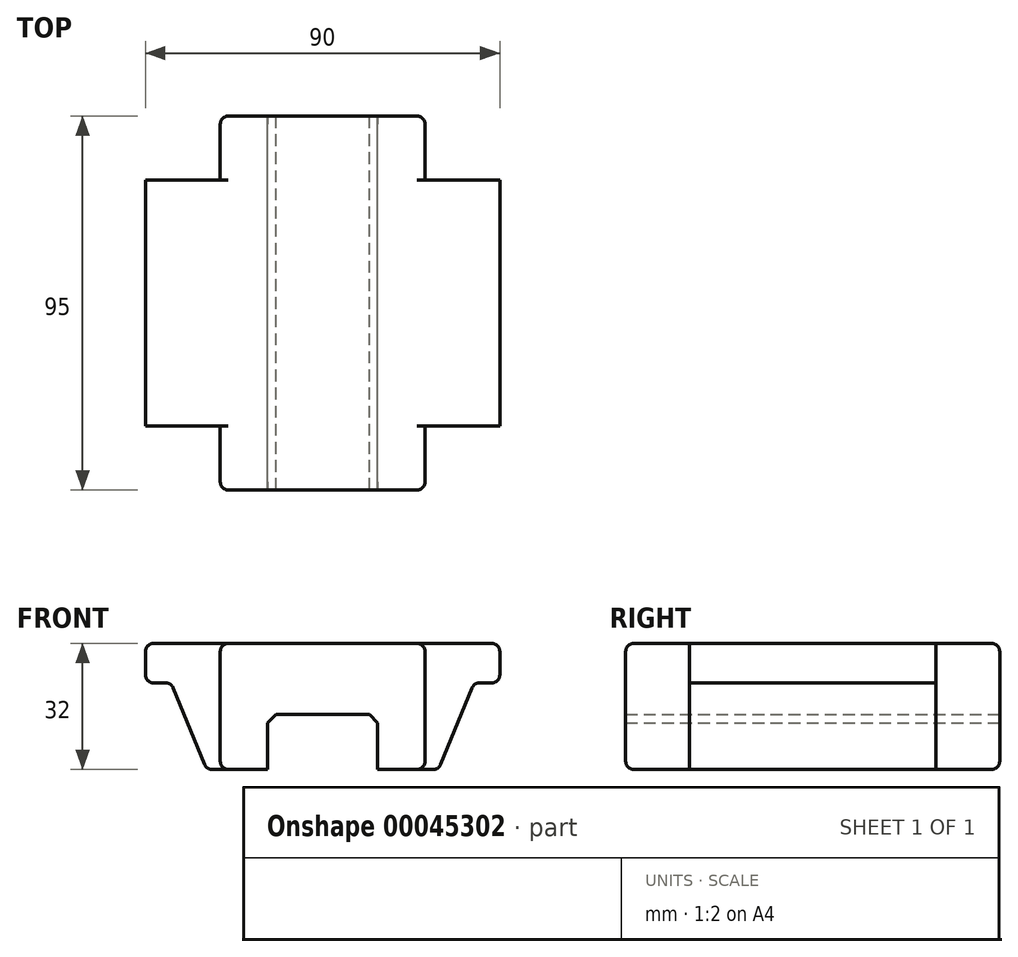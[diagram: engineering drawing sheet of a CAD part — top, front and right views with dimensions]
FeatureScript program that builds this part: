
annotation { "Feature Type Name" : "Feature", "Feature Type Description" : "" }
export const myFeature = defineFeature(function(context is Context, id is Id, definition is map)
    precondition{}
    {
        {
            var Q0;
            Q0=qCreatedBy(makeId("Front.planeOp"),FACE);
            var sketch = newSketch(context, id + "F0", { "sketchPlane" : qUnion([Q0])});
            skLineSegment(sketch, "E0.bottom", {"start": v(-47.43, 10.94) * mm, "end": v(42.57, 10.94) * mm});
            skLineSegment(sketch, "E0.top", {"start": v(-47.43, -21.06) * mm, "end": v(42.57, -21.06) * mm});
            skLineSegment(sketch, "E0.left", {"start": v(-47.43, 10.94) * mm, "end": v(-47.43, -21.06) * mm});
            skLineSegment(sketch, "E0.right", {"start": v(42.57, 10.94) * mm, "end": v(42.57, -21.06) * mm});
            skSolve(sketch);
        }
        {
            var Q0;
            Q0 = qSketchRegion(id + "F0", true);
            extrude(context, id + "F1", {"entities" : qUnion([Q0]), "depth" : 65.2 * mm});
        }
        {
            var Q0;
            Q0=makeQuery(id+"F1.opExtrude","CAP_FACE",FACE,{"disambiguationData":[OSD([sQuery(id+"F0.wireOp",EDGE,"E0.bottom"),sQuery(id+"F0.wireOp",EDGE,"E0.top"),sQuery(id+"F0.wireOp",EDGE,"E0.left"),sQuery(id+"F0.wireOp",EDGE,"E0.right")])],"isStart":false});
            var sketch = newSketch(context, id + "F2", { "sketchPlane" : qUnion([Q0])});
            skLineSegment(sketch, "E1.bottom", {"start": v(-45.43, 10.94) * mm, "end": v(40.57, 10.94) * mm});
            skLineSegment(sketch, "E1.top", {"start": v(-45.43, 0.94) * mm, "end": v(-42.27, 0.94) * mm});
            skLineSegment(sketch, "E1.left", {"start": v(-47.43, 8.94) * mm, "end": v(-47.43, 2.94) * mm});
            skLineSegment(sketch, "E1.right", {"start": v(42.57, 8.94) * mm, "end": v(42.57, 2.94) * mm});
            skLineSegment(sketch, "E2.top", {"start": v(-30.59, -21.06) * mm, "end": v(25.73, -21.06) * mm});
            skLineSegment(sketch, "E3", {"start": v(-40.42, -0.3) * mm, "end": v(-32.44, -19.82) * mm});
            skLineSegment(sketch, "E4", {"start": v(27.58, -19.82) * mm, "end": v(35.56, -0.3) * mm});
            skLineSegment(sketch, "E5.trimOffspring", {"start": v(37.41, 0.94) * mm, "end": v(40.57, 0.94) * mm});
            skPoint(sketch, "E6.visualSharp", {"position": v(42.57, 0.94) * mm});
            skArc(sketch, "E6.filletArc", {"start": v(40.57, 0.94) * mm, "mid": v(41.98, 1.53) * mm, "end": v(42.57, 2.94) * mm});
            skPoint(sketch, "E7.visualSharp", {"position": v(42.57, 10.94) * mm});
            skArc(sketch, "E7.filletArc", {"start": v(42.57, 8.94) * mm, "mid": v(41.98, 10.36) * mm, "end": v(40.57, 10.94) * mm});
            skPoint(sketch, "E8.visualSharp", {"position": v(36.07, 0.94) * mm});
            skArc(sketch, "E8.filletArc", {"start": v(37.41, 0.94) * mm, "mid": v(36.3, 0.6) * mm, "end": v(35.56, -0.3) * mm});
            skPoint(sketch, "E9.visualSharp", {"position": v(27.07, -21.06) * mm});
            skArc(sketch, "E9.filletArc", {"start": v(25.73, -21.06) * mm, "mid": v(26.84, -20.72) * mm, "end": v(27.58, -19.82) * mm});
            skPoint(sketch, "E10.visualSharp", {"position": v(-31.93, -21.06) * mm});
            skArc(sketch, "E10.filletArc", {"start": v(-32.44, -19.82) * mm, "mid": v(-31.7, -20.72) * mm, "end": v(-30.59, -21.06) * mm});
            skPoint(sketch, "E11.visualSharp", {"position": v(-40.93, 0.94) * mm});
            skArc(sketch, "E11.filletArc", {"start": v(-40.42, -0.3) * mm, "mid": v(-41.16, 0.6) * mm, "end": v(-42.27, 0.94) * mm});
            skPoint(sketch, "E12.visualSharp", {"position": v(-47.43, 0.94) * mm});
            skArc(sketch, "E12.filletArc", {"start": v(-47.43, 2.94) * mm, "mid": v(-46.84, 1.53) * mm, "end": v(-45.43, 0.94) * mm});
            skPoint(sketch, "E13.visualSharp", {"position": v(-47.43, 10.94) * mm});
            skArc(sketch, "E13.filletArc", {"start": v(-45.43, 10.94) * mm, "mid": v(-46.84, 10.36) * mm, "end": v(-47.43, 8.94) * mm});
            skSolve(sketch);
        }
        {
            var Q0;
            Q0 = qSketchRegion(id + "F2", true);
            extrude(context, id + "F3", {"entities" : qUnion([Q0]), "operationType" : NewBodyOperationType.ADD, "depth" : 25 * mm});
        }
        {
            var Q0;
            Q0=makeQuery(id+"F3.boolean.opBoolean","MERGE",FACE,{"derivedFrom":[makeQuery(id+"F1.opExtrude","SWEPT_FACE",FACE,{"disambiguationData":[OSD([sQuery(id+"F0.wireOp",EDGE,"E0.bottom")])]}),makeQuery(id+"F3.opExtrude","SWEPT_FACE",FACE,{"disambiguationData":[OSD([sQuery(id+"F2.wireOp",EDGE,"E1.bottom")])]})]});
            var sketch = newSketch(context, id + "F4", { "sketchPlane" : qUnion([Q0])});
            skLineSegment(sketch, "E14.bottom", {"start": v(-47.43, 0) * mm, "end": v(42.57, 0) * mm});
            skLineSegment(sketch, "E14.top", {"start": v(-47.43, -65.2) * mm, "end": v(42.57, -65.2) * mm});
            skLineSegment(sketch, "E14.left", {"start": v(-47.43, 0) * mm, "end": v(-47.43, -65.2) * mm});
            skLineSegment(sketch, "E14.right", {"start": v(42.57, 0) * mm, "end": v(42.57, -65.2) * mm});
            skSolve(sketch);
        }
        {
            var Q0;
            Q0 = qSketchRegion(id + "F4", true);
            extrude(context, id + "F5", {"entities" : qUnion([Q0]), "operationType" : NewBodyOperationType.REMOVE, "endBound" : BoundingType.THROUGH_ALL, "oppositeDirection" : true, "depth" : 25 * mm});
        }
        {
            var Q0;
            Q0=makeQuery(id+"F3.opExtrude","CAP_FACE",FACE,{"disambiguationData":[OSD([sQuery(id+"F2.wireOp",EDGE,"E1.bottom"),sQuery(id+"F2.wireOp",EDGE,"E1.top"),sQuery(id+"F2.wireOp",EDGE,"E1.left"),sQuery(id+"F2.wireOp",EDGE,"E1.right"),sQuery(id+"F2.wireOp",EDGE,"E2.top"),sQuery(id+"F2.wireOp",EDGE,"E3"),sQuery(id+"F2.wireOp",EDGE,"E4"),sQuery(id+"F2.wireOp",EDGE,"E5.trimOffspring"),sQuery(id+"F2.wireOp",EDGE,"E6.filletArc"),sQuery(id+"F2.wireOp",EDGE,"E7.filletArc"),sQuery(id+"F2.wireOp",EDGE,"E8.filletArc"),sQuery(id+"F2.wireOp",EDGE,"E9.filletArc"),sQuery(id+"F2.wireOp",EDGE,"E10.filletArc"),sQuery(id+"F2.wireOp",EDGE,"E11.filletArc"),sQuery(id+"F2.wireOp",EDGE,"E12.filletArc"),sQuery(id+"F2.wireOp",EDGE,"E13.filletArc")])],"isStart":false});
            extrude(context, id + "F6", {"entities" : qUnion([Q0]), "operationType" : NewBodyOperationType.ADD, "oppositeDirection" : true, "depth" : 62.5 * mm});
        }
        {
            var Q0;
            Q0=makeQuery(id+"F3.opExtrude","CAP_FACE",FACE,{"disambiguationData":[OSD([sQuery(id+"F2.wireOp",EDGE,"E1.bottom"),sQuery(id+"F2.wireOp",EDGE,"E1.top"),sQuery(id+"F2.wireOp",EDGE,"E1.left"),sQuery(id+"F2.wireOp",EDGE,"E1.right"),sQuery(id+"F2.wireOp",EDGE,"E2.top"),sQuery(id+"F2.wireOp",EDGE,"E3"),sQuery(id+"F2.wireOp",EDGE,"E4"),sQuery(id+"F2.wireOp",EDGE,"E5.trimOffspring"),sQuery(id+"F2.wireOp",EDGE,"E6.filletArc"),sQuery(id+"F2.wireOp",EDGE,"E7.filletArc"),sQuery(id+"F2.wireOp",EDGE,"E8.filletArc"),sQuery(id+"F2.wireOp",EDGE,"E9.filletArc"),sQuery(id+"F2.wireOp",EDGE,"E10.filletArc"),sQuery(id+"F2.wireOp",EDGE,"E11.filletArc"),sQuery(id+"F2.wireOp",EDGE,"E12.filletArc"),sQuery(id+"F2.wireOp",EDGE,"E13.filletArc")])],"isStart":false});
            var sketch = newSketch(context, id + "F7", { "sketchPlane" : qUnion([Q0])});
            skLineSegment(sketch, "E15.bottom", {"start": v(-26.43, 10.94) * mm, "end": v(21.57, 10.94) * mm});
            skLineSegment(sketch, "E15.top", {"start": v(-26.43, -21.06) * mm, "end": v(-16.43, -21.06) * mm});
            skLineSegment(sketch, "E15.left", {"start": v(-28.43, 8.94) * mm, "end": v(-28.43, -19.06) * mm});
            skLineSegment(sketch, "E15.right", {"start": v(23.57, 8.94) * mm, "end": v(23.57, -19.06) * mm});
            skPoint(sketch, "E16.visualSharp", {"position": v(-28.43, 10.94) * mm});
            skArc(sketch, "E16.filletArc", {"start": v(-26.43, 10.94) * mm, "mid": v(-27.84, 10.36) * mm, "end": v(-28.43, 8.94) * mm});
            skPoint(sketch, "E17.visualSharp", {"position": v(23.57, 10.94) * mm});
            skArc(sketch, "E17.filletArc", {"start": v(23.57, 8.94) * mm, "mid": v(22.98, 10.36) * mm, "end": v(21.57, 10.94) * mm});
            skPoint(sketch, "E18.visualSharp", {"position": v(23.57, -21.06) * mm});
            skArc(sketch, "E18.filletArc", {"start": v(21.57, -21.06) * mm, "mid": v(22.98, -20.47) * mm, "end": v(23.57, -19.06) * mm});
            skPoint(sketch, "E19.visualSharp", {"position": v(-28.43, -21.06) * mm});
            skArc(sketch, "E19.filletArc", {"start": v(-28.43, -19.06) * mm, "mid": v(-27.84, -20.47) * mm, "end": v(-26.43, -21.06) * mm});
            skLineSegment(sketch, "E20.top", {"start": v(-14.3, -7.06) * mm, "end": v(9.45, -7.06) * mm});
            skLineSegment(sketch, "E20.left", {"start": v(-16.43, -21.06) * mm, "end": v(-16.43, -9.18) * mm});
            skLineSegment(sketch, "E20.right", {"start": v(11.57, -21.06) * mm, "end": v(11.57, -9.18) * mm});
            skLineSegment(sketch, "E21", {"start": v(-16.43, -9.18) * mm, "end": v(-14.3, -7.06) * mm});
            skLineSegment(sketch, "E22", {"start": v(9.45, -7.06) * mm, "end": v(11.57, -9.18) * mm});
            skLineSegment(sketch, "E23.trimOffspring", {"start": v(11.57, -21.06) * mm, "end": v(21.57, -21.06) * mm});
            skSolve(sketch);
        }
        {
            var Q0;
            Q0=makeQuery(id+"F7.imprint","IMPRINT",FACE,{"disambiguationData":[TD([[makeQuery(id+"F7.imprint","IMPRINT",EDGE,{"derivedFrom":sQuery(id+"F7.wireOp",EDGE,"E15.bottom")}),-1.0]])]});
            extrude(context, id + "F8", {"entities" : qUnion([Q0]), "operationType" : NewBodyOperationType.ADD, "depth" : 16.25 * mm, "hasSecondDirection" : true, "secondDirectionOppositeDirection" : true, "secondDirectionDepth" : 78.75 * mm});
        }
        {
            var Q0;
            Q0=makeQuery(id+"F8.opExtrude","CAP_EDGE",EDGE,{"disambiguationData":[OSD([sQuery(id+"F7.wireOp",EDGE,"E15.left")])],"isStart":false});
            var Q1;
            Q1=makeQuery(id+"F8.opExtrude","CAP_EDGE",EDGE,{"disambiguationData":[OSD([sQuery(id+"F7.wireOp",EDGE,"E15.bottom")])],"isStart":true});
            fillet(context, id + "F9", {"entities" : qUnion([Q0, Q1]), "radius" : 2 * mm, "tangentPropagation" : true, "allowEdgeOverflow" : false});
        }
        {
            var Q0;
            {var subQ0=sQuery(id+"F2.wireOp",EDGE,"E2.top");Q0=makeQuery(id+"F8.boolean.opBoolean","SPLIT",FACE,{"disambiguationData":[TD([makeQuery(id+"F8.opExtrude","SWEPT_FACE",FACE,{"disambiguationData":[OSD([sQuery(id+"F7.wireOp",EDGE,"E20.top")])]})])],"derivedFrom":makeQuery(id+"F3.opExtrude","CAP_FACE",FACE,{"disambiguationData":[OSD([sQuery(id+"F2.wireOp",EDGE,"E1.bottom"),sQuery(id+"F2.wireOp",EDGE,"E1.top"),sQuery(id+"F2.wireOp",EDGE,"E1.left"),sQuery(id+"F2.wireOp",EDGE,"E1.right"),subQ0,sQuery(id+"F2.wireOp",EDGE,"E3"),sQuery(id+"F2.wireOp",EDGE,"E4"),sQuery(id+"F2.wireOp",EDGE,"E5.trimOffspring"),sQuery(id+"F2.wireOp",EDGE,"E6.filletArc"),sQuery(id+"F2.wireOp",EDGE,"E7.filletArc"),sQuery(id+"F2.wireOp",EDGE,"E8.filletArc"),sQuery(id+"F2.wireOp",EDGE,"E9.filletArc"),sQuery(id+"F2.wireOp",EDGE,"E10.filletArc"),sQuery(id+"F2.wireOp",EDGE,"E11.filletArc"),sQuery(id+"F2.wireOp",EDGE,"E12.filletArc"),sQuery(id+"F2.wireOp",EDGE,"E13.filletArc")])],"isStart":false})});}
            var sketch = newSketch(context, id + "F10", { "sketchPlane" : qUnion([Q0])});
            skLineSegment(sketch, "E24", {"start": v(-16.43, -21.06) * mm, "end": v(-16.43, -9.18) * mm});
            skLineSegment(sketch, "E25", {"start": v(-16.43, -9.18) * mm, "end": v(-14.3, -7.06) * mm});
            skLineSegment(sketch, "E26", {"start": v(-14.3, -7.06) * mm, "end": v(9.45, -7.06) * mm});
            skLineSegment(sketch, "E27", {"start": v(9.45, -7.06) * mm, "end": v(11.57, -9.18) * mm});
            skLineSegment(sketch, "E28", {"start": v(11.57, -9.18) * mm, "end": v(11.57, -21.06) * mm});
            skLineSegment(sketch, "E29", {"start": v(11.57, -21.06) * mm, "end": v(-16.43, -21.06) * mm});
            skSolve(sketch);
        }
        {
            var Q0;
            Q0 = qSketchRegion(id + "F10", true);
            extrude(context, id + "F11", {"entities" : qUnion([Q0]), "operationType" : NewBodyOperationType.REMOVE, "endBound" : BoundingType.THROUGH_ALL, "oppositeDirection" : true, "depth" : 25 * mm});
        }
    });
